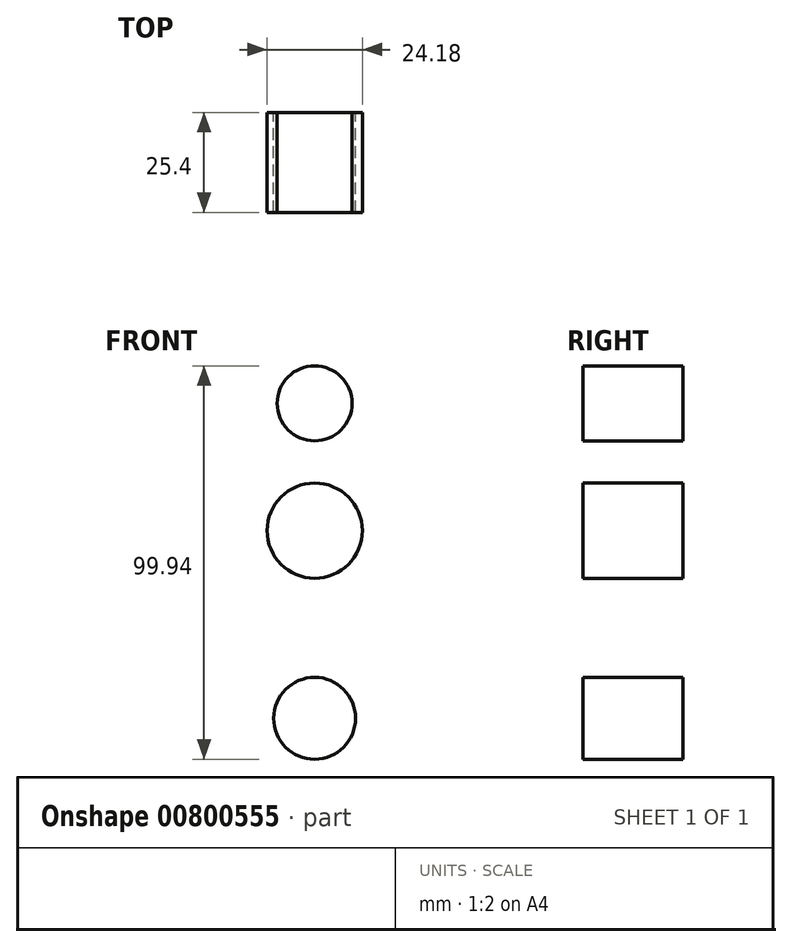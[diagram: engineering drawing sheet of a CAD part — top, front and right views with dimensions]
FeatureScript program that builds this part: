
annotation { "Feature Type Name" : "Feature", "Feature Type Description" : "" }
export const myFeature = defineFeature(function(context is Context, id is Id, definition is map)
    precondition{}
    {
        {
            var Q0;
            Q0=qCreatedBy(makeId("Front.planeOp"),FACE);
            var sketch = newSketch(context, id + "F0", { "sketchPlane" : qUnion([Q0])});
            skLineSegment(sketch, "E0", {"start": v(0, 80.01) * mm, "end": v(0, 0) * mm});
            skLineSegment(sketch, "E1", {"start": v(0, 0) * mm, "end": v(56.53, 0) * mm});
            skCircle(sketch, "E2", {"center": v(0, 80.01) * mm, "radius": 9.53 * mm});
            skCircle(sketch, "E3", {"center": v(0, 47.68) * mm, "radius": 12.1 * mm});
            skCircle(sketch, "E4", {"center": v(0, 0) * mm, "radius": 10.4 * mm});
            skSolve(sketch);
        }
        {
            var Q0;
            Q0 = qSketchRegion(id + "F0", true);
            extrude(context, id + "F1", {"entities" : qUnion([Q0]), "depth" : 25.4 * mm, "offsetDistance" : 25.4 * mm});
        }
    });
